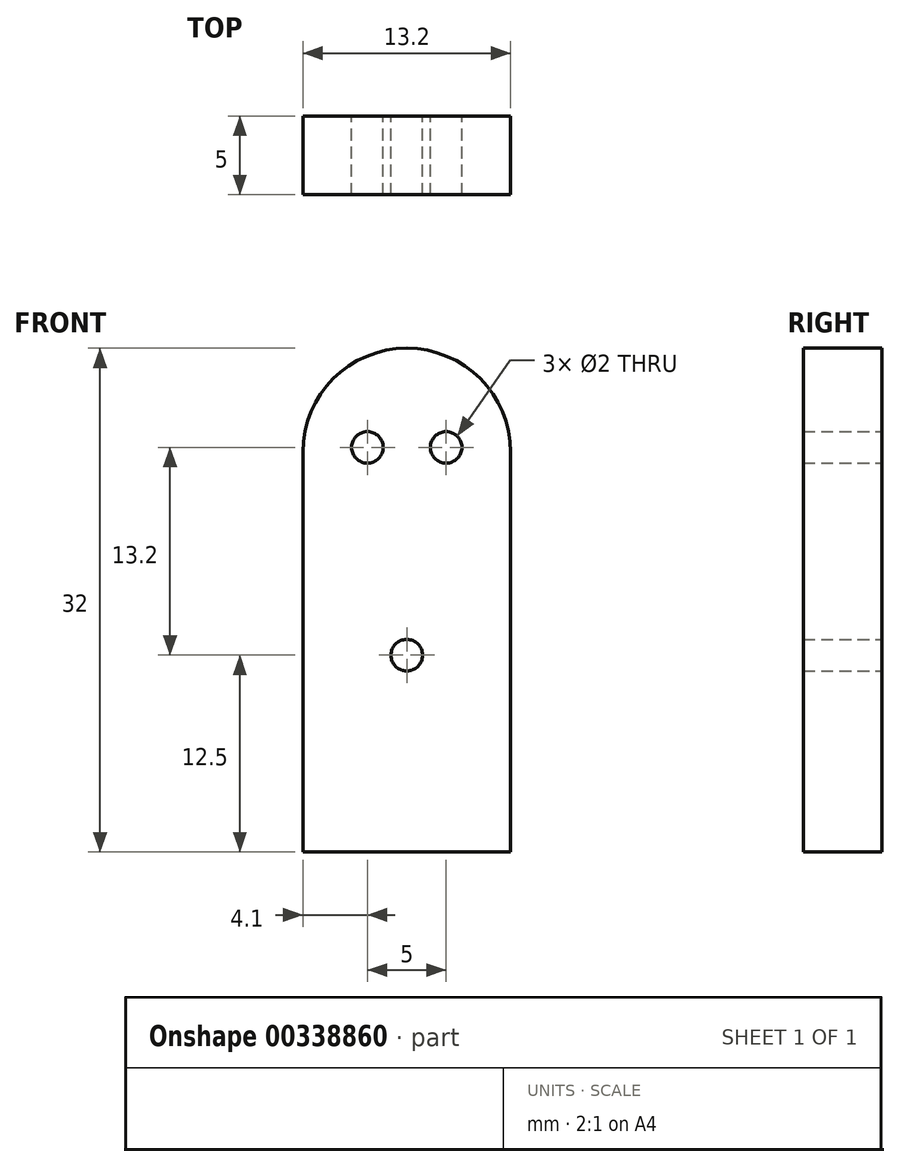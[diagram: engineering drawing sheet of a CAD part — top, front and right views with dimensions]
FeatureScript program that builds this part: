
annotation { "Feature Type Name" : "Feature", "Feature Type Description" : "" }
export const myFeature = defineFeature(function(context is Context, id is Id, definition is map)
    precondition{}
    {
        {
            var Q0;
            Q0=qCreatedBy(makeId("Front.planeOp"),FACE);
            var sketch = newSketch(context, id + "F0", { "sketchPlane" : qUnion([Q0])});
            skLineSegment(sketch, "E0.bottom", {"start": v(0, 0) * mm, "end": v(13.2, 0) * mm});
            skLineSegment(sketch, "E0.left", {"start": v(0, 0) * mm, "end": v(0, 25.4) * mm});
            skLineSegment(sketch, "E0.right", {"start": v(13.2, 0) * mm, "end": v(13.2, 25.4) * mm});
            skArc(sketch, "E1", {"start": v(13.2, 25.4) * mm, "mid": v(6.6, 32) * mm, "end": v(0, 25.4) * mm});
            skCircle(sketch, "E2", {"center": v(4.1, 25.7) * mm, "radius": 1 * mm});
            skCircle(sketch, "E3", {"center": v(9.1, 25.7) * mm, "radius": 1 * mm});
            skCircle(sketch, "E4", {"center": v(6.6, 12.5) * mm, "radius": 1 * mm});
            skSolve(sketch);
        }
        {
            var Q0;
            Q0=makeQuery(id+"F0.imprint","IMPRINT",FACE,{"disambiguationData":[TD([[makeQuery(id+"F0.imprint","IMPRINT",EDGE,{"derivedFrom":sQuery(id+"F0.wireOp",EDGE,"E0.bottom")}),1.0]])]});
            extrude(context, id + "F1", {"entities" : qUnion([Q0]), "depth" : 5 * mm});
        }
    });
